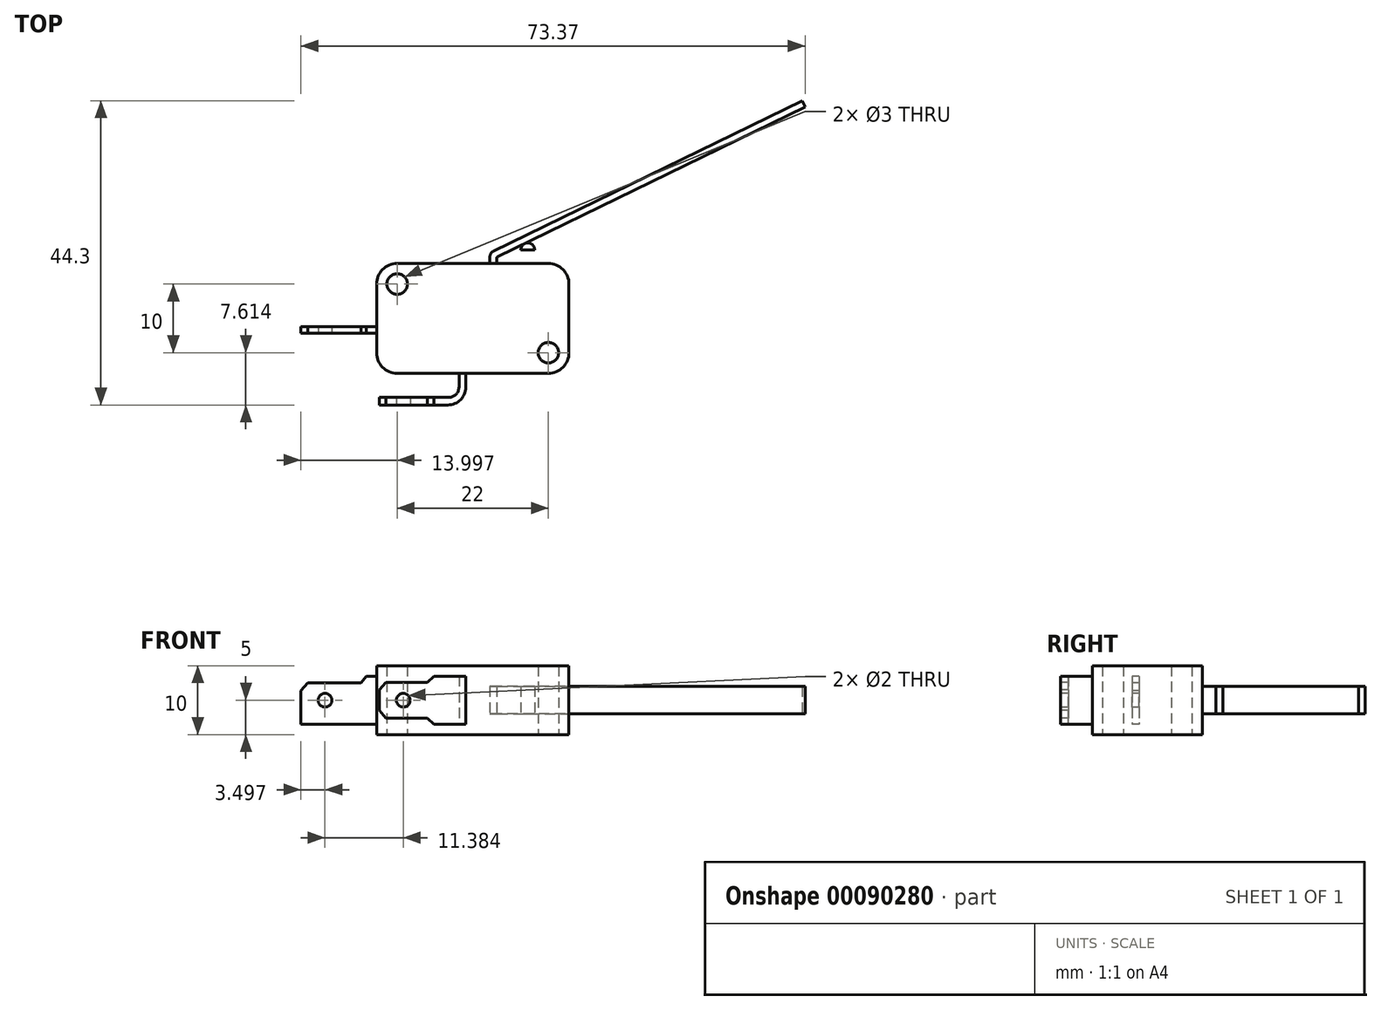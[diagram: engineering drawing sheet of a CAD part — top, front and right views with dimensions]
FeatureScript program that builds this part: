
annotation { "Feature Type Name" : "Feature", "Feature Type Description" : "" }
export const myFeature = defineFeature(function(context is Context, id is Id, definition is map)
    precondition{}
    {
        {
            var Q0;
            Q0=qCreatedBy(makeId("Top.planeOp"),FACE);
            var sketch = newSketch(context, id + "F0", { "sketchPlane" : qUnion([Q0])});
            skLineSegment(sketch, "E0.bottom", {"start": v(11.18, -8.94) * mm, "end": v(33.18, -8.94) * mm});
            skLineSegment(sketch, "E0.top", {"start": v(11.18, -24.94) * mm, "end": v(33.18, -24.94) * mm});
            skLineSegment(sketch, "E0.left", {"start": v(8.18, -11.94) * mm, "end": v(8.18, -21.94) * mm});
            skLineSegment(sketch, "E0.right", {"start": v(36.18, -11.94) * mm, "end": v(36.18, -21.94) * mm});
            skPoint(sketch, "E1.visualSharp", {"position": v(8.18, -8.94) * mm});
            skArc(sketch, "E1.filletArc", {"start": v(11.18, -8.94) * mm, "mid": v(9.06, -9.81) * mm, "end": v(8.18, -11.94) * mm});
            skPoint(sketch, "E2.visualSharp", {"position": v(8.18, -24.94) * mm});
            skArc(sketch, "E2.filletArc", {"start": v(8.18, -21.94) * mm, "mid": v(9.06, -24.06) * mm, "end": v(11.18, -24.94) * mm});
            skPoint(sketch, "E3.visualSharp", {"position": v(36.18, -24.94) * mm});
            skArc(sketch, "E3.filletArc", {"start": v(33.18, -24.94) * mm, "mid": v(35.3, -24.06) * mm, "end": v(36.18, -21.94) * mm});
            skPoint(sketch, "E4.visualSharp", {"position": v(36.18, -8.94) * mm});
            skArc(sketch, "E4.filletArc", {"start": v(36.18, -11.94) * mm, "mid": v(35.3, -9.81) * mm, "end": v(33.18, -8.94) * mm});
            skCircle(sketch, "E5", {"center": v(11.18, -11.94) * mm, "radius": 1.5 * mm});
            skCircle(sketch, "E6", {"center": v(33.18, -21.94) * mm, "radius": 1.5 * mm});
            skLineSegment(sketch, "E7.bottom", {"start": v(29.18, -8.94) * mm, "end": v(31.18, -8.94) * mm});
            skLineSegment(sketch, "E7.top", {"start": v(29.18, -6.94) * mm, "end": v(31.18, -6.94) * mm});
            skLineSegment(sketch, "E7.left", {"start": v(29.18, -8.94) * mm, "end": v(29.18, -6.94) * mm});
            skLineSegment(sketch, "E7.right", {"start": v(31.18, -8.94) * mm, "end": v(31.18, -6.94) * mm});
            skArc(sketch, "E8", {"start": v(31.18, -6.94) * mm, "mid": v(30.18, -5.94) * mm, "end": v(29.18, -6.94) * mm});
            skLineSegment(sketch, "E9", {"start": v(25.68, -8.94) * mm, "end": v(25.68, -8.1) * mm});
            skLineSegment(sketch, "E10", {"start": v(25.76, -7.98) * mm, "end": v(70.55, 13.85) * mm});
            skLineSegment(sketch, "E11", {"start": v(70.55, 13.85) * mm, "end": v(70.12, 14.75) * mm});
            skLineSegment(sketch, "E12", {"start": v(70.12, 14.75) * mm, "end": v(25.17, -7.15) * mm});
            skLineSegment(sketch, "E13", {"start": v(24.68, -7.94) * mm, "end": v(24.68, -8.94) * mm});
            skPoint(sketch, "E14.visualSharp", {"position": v(24.68, -7.4) * mm});
            skArc(sketch, "E14.filletArc", {"start": v(25.17, -7.15) * mm, "mid": v(24.8, -7.47) * mm, "end": v(24.68, -7.94) * mm});
            skPoint(sketch, "E15.visualSharp", {"position": v(25.68, -8.02) * mm});
            skArc(sketch, "E15.filletArc", {"start": v(25.76, -7.98) * mm, "mid": v(25.7, -8.03) * mm, "end": v(25.68, -8.1) * mm});
            skLineSegment(sketch, "E16.bottom", {"start": v(8.18, -19.12) * mm, "end": v(-2.82, -19.12) * mm});
            skLineSegment(sketch, "E16.top", {"start": v(8.18, -18.12) * mm, "end": v(-2.82, -18.12) * mm});
            skLineSegment(sketch, "E16.left", {"start": v(8.18, -19.12) * mm, "end": v(8.18, -18.12) * mm});
            skLineSegment(sketch, "E16.right", {"start": v(-2.82, -19.12) * mm, "end": v(-2.82, -18.12) * mm});
            skLineSegment(sketch, "E17", {"start": v(21.18, -24.94) * mm, "end": v(21.18, -26.94) * mm});
            skLineSegment(sketch, "E18", {"start": v(18.56, -29.55) * mm, "end": v(8.56, -29.55) * mm});
            skLineSegment(sketch, "E19", {"start": v(8.56, -29.55) * mm, "end": v(8.56, -28.44) * mm});
            skLineSegment(sketch, "E20", {"start": v(8.56, -28.44) * mm, "end": v(18.68, -28.44) * mm});
            skLineSegment(sketch, "E21", {"start": v(20.18, -26.94) * mm, "end": v(20.18, -24.94) * mm});
            skPoint(sketch, "E22.visualSharp", {"position": v(21.18, -29.55) * mm});
            skArc(sketch, "E22.filletArc", {"start": v(18.56, -29.55) * mm, "mid": v(20.41, -28.79) * mm, "end": v(21.18, -26.94) * mm});
            skPoint(sketch, "E23.visualSharp", {"position": v(20.18, -28.44) * mm});
            skArc(sketch, "E23.filletArc", {"start": v(18.68, -28.44) * mm, "mid": v(19.74, -28) * mm, "end": v(20.18, -26.94) * mm});
            skLineSegment(sketch, "E24", {"start": v(15.13, -28.44) * mm, "end": v(15.13, -24.94) * mm});
            skSolve(sketch);
        }
        {
            var Q0;
            Q0=makeQuery(id+"F0.imprint","IMPRINT",FACE,{"disambiguationData":[TD([[makeQuery(id+"F0.imprint","IMPRINT",EDGE,{"derivedFrom":sQuery(id+"F0.wireOp",EDGE,"E0.right")}),-1.0]])]});
            extrude(context, id + "F1", {"entities" : qUnion([Q0]), "depth" : 5 * mm, "hasSecondDirection" : true, "secondDirectionOppositeDirection" : true, "secondDirectionDepth" : 5 * mm});
        }
        {
            var Q0;
            Q0=makeQuery(id+"F0.imprint","IMPRINT",FACE,{"disambiguationData":[TD([[makeQuery(id+"F0.imprint","IMPRINT",EDGE,{"derivedFrom":sQuery(id+"F0.wireOp",EDGE,"E7.bottom")}),1.0]])]});
            var Q1;
            {var subQ0=sQuery(id+"F0.wireOp",EDGE,"E7.top");Q1=makeQuery(id+"F0.imprint","IMPRINT",FACE,{"disambiguationData":[TD([[makeQuery(id+"F0.imprint","IMPRINT",EDGE,{"derivedFrom":subQ0}),1.0]])]});}
            extrude(context, id + "F2", {"entities" : qUnion([Q0, Q1]), "depth" : 2 * mm, "hasSecondDirection" : true, "secondDirectionOppositeDirection" : true, "secondDirectionDepth" : 2 * mm});
        }
        {
            var Q0;
            {var subQ4=sQuery(id+"F0.wireOp",EDGE,"E9");Q0=makeQuery(id+"F0.imprint","IMPRINT",FACE,{"disambiguationData":[TD([[makeQuery(id+"F0.imprint","IMPRINT",EDGE,{"derivedFrom":subQ4}),1.0]])]});}
            extrude(context, id + "F3", {"entities" : qUnion([Q0]), "depth" : 2 * mm, "hasSecondDirection" : true, "secondDirectionOppositeDirection" : true, "secondDirectionDepth" : 2 * mm});
        }
        {
            var Q0;
            {var subQ1=sQuery(id+"F0.wireOp",EDGE,"E17");Q0=makeQuery(id+"F0.imprint","IMPRINT",FACE,{"disambiguationData":[TD([[makeQuery(id+"F0.imprint","IMPRINT",EDGE,{"derivedFrom":subQ1}),-1.0]])]});}
            extrude(context, id + "F4", {"entities" : qUnion([Q0]), "depth" : 3.5 * mm, "hasSecondDirection" : true, "secondDirectionOppositeDirection" : true, "secondDirectionDepth" : 3.5 * mm});
        }
        {
            var Q0;
            Q0=makeQuery(id+"F0.imprint","IMPRINT",FACE,{"disambiguationData":[TD([[makeQuery(id+"F0.imprint","IMPRINT",EDGE,{"derivedFrom":sQuery(id+"F0.wireOp",EDGE,"E16.bottom")}),-1.0]])]});
            extrude(context, id + "F5", {"entities" : qUnion([Q0]), "depth" : 3.5 * mm, "hasSecondDirection" : true, "secondDirectionOppositeDirection" : true, "secondDirectionDepth" : 3.5 * mm});
        }
        {
            var Q0;
            Q0=makeQuery(id+"F4.opExtrude","SWEPT_FACE",FACE,{"disambiguationData":[OSD([sQuery(id+"F0.wireOp",EDGE,"E18")])]});
            var sketch = newSketch(context, id + "F6", { "sketchPlane" : qUnion([Q0])});
            skCircle(sketch, "E25", {"center": v(12.06, 0) * mm, "radius": 1 * mm});
            skLineSegment(sketch, "E26", {"start": v(16.52, 3.5) * mm, "end": v(15.56, 2.62) * mm});
            skLineSegment(sketch, "E27", {"start": v(15.56, 2.62) * mm, "end": v(9.56, 2.62) * mm});
            skLineSegment(sketch, "E28", {"start": v(9.56, 2.62) * mm, "end": v(8.56, 1.5) * mm});
            skLineSegment(sketch, "E29", {"start": v(8.56, 1.5) * mm, "end": v(8.56, -1.5) * mm});
            skLineSegment(sketch, "E30", {"start": v(8.56, -1.5) * mm, "end": v(9.56, -2.62) * mm});
            skLineSegment(sketch, "E31", {"start": v(9.56, -2.62) * mm, "end": v(15.56, -2.62) * mm});
            skLineSegment(sketch, "E32", {"start": v(15.56, -2.62) * mm, "end": v(16.52, -3.5) * mm});
            skSolve(sketch);
        }
        {
            var Q0;
            {var subQ4=sQuery(id+"F6.wireOp",EDGE,"E30");Q0=makeQuery(id+"F6.imprint","IMPRINT",FACE,{"disambiguationData":[TD([[makeQuery(id+"F6.imprint","IMPRINT",EDGE,{"derivedFrom":subQ4}),-1.0]])]});}
            var Q1;
            {var subQ5=sQuery(id+"F6.wireOp",EDGE,"E26");Q1=makeQuery(id+"F6.imprint","IMPRINT",FACE,{"disambiguationData":[TD([[makeQuery(id+"F6.imprint","IMPRINT",EDGE,{"derivedFrom":subQ5}),-1.0]])]});}
            var Q2;
            Q2=makeQuery(id+"F6.imprint","IMPRINT",FACE,{"disambiguationData":[TD([[makeQuery(id+"F6.imprint","IMPRINT",EDGE,{"derivedFrom":sQuery(id+"F6.wireOp",EDGE,"E25")}),1.0]])]});
            extrude(context, id + "F7", {"entities" : qUnion([Q0, Q1, Q2]), "operationType" : NewBodyOperationType.REMOVE, "oppositeDirection" : true, "depth" : 3.08 * mm});
        }
        {
            var Q0;
            Q0=makeQuery(id+"F4.opExtrude","SWEPT_FACE",FACE,{"disambiguationData":[OSD([sQuery(id+"F0.wireOp",EDGE,"E18")])]});
            var sketch = newSketch(context, id + "F8", { "sketchPlane" : qUnion([Q0])});
            skCircle(sketch, "E33", {"center": v(0.68, 0) * mm, "radius": 1 * mm});
            skLineSegment(sketch, "E34", {"start": v(8.18, -3.5) * mm, "end": v(8.18, 3.5) * mm});
            skLineSegment(sketch, "E35", {"start": v(8.18, 3.5) * mm, "end": v(6.68, 3.5) * mm});
            skLineSegment(sketch, "E36", {"start": v(6.68, 3.5) * mm, "end": v(5.93, 2.5) * mm});
            skLineSegment(sketch, "E37", {"start": v(5.93, 2.5) * mm, "end": v(-1.82, 2.5) * mm});
            skLineSegment(sketch, "E38", {"start": v(-1.82, 2.5) * mm, "end": v(-2.82, 1.37) * mm});
            skLineSegment(sketch, "E39", {"start": v(-2.82, 1.37) * mm, "end": v(-2.82, -1.38) * mm});
            skLineSegment(sketch, "E40", {"start": v(-2.82, -1.38) * mm, "end": v(-1.82, -2.5) * mm});
            skLineSegment(sketch, "E41", {"start": v(-1.82, -2.5) * mm, "end": v(5.93, -2.5) * mm});
            skLineSegment(sketch, "E42", {"start": v(5.93, -2.5) * mm, "end": v(6.68, -3.5) * mm});
            skLineSegment(sketch, "E43", {"start": v(6.68, -3.5) * mm, "end": v(8.18, -3.5) * mm});
            skLineSegment(sketch, "E44", {"start": v(6.68, 3.5) * mm, "end": v(-2.82, 3.5) * mm});
            skLineSegment(sketch, "E45", {"start": v(-2.82, 3.5) * mm, "end": v(-2.82, 1.37) * mm});
            skLineSegment(sketch, "E46", {"start": v(-2.82, -1.38) * mm, "end": v(-2.82, -3.5) * mm});
            skLineSegment(sketch, "E47", {"start": v(-2.82, -3.5) * mm, "end": v(6.68, -3.5) * mm});
            skLineSegment(sketch, "E48", {"start": v(5.93, -2.5) * mm, "end": v(-1.82, -2.5) * mm});
            skLineSegment(sketch, "E49", {"start": v(6.68, -3.5) * mm, "end": v(-2.82, -3.5) * mm});
            skLineSegment(sketch, "E50", {"start": v(-2.82, -3.5) * mm, "end": v(-2.82, -1.38) * mm});
            skSolve(sketch);
        }
        {
            var Q0;
            Q0=makeQuery(id+"F8.imprint","IMPRINT",FACE,{"disambiguationData":[TD([[makeQuery(id+"F8.imprint","IMPRINT",EDGE,{"derivedFrom":sQuery(id+"F8.wireOp",EDGE,"E36")}),-1.0]])]});
            var Q1;
            Q1=makeQuery(id+"F8.imprint","IMPRINT",FACE,{"disambiguationData":[TD([[makeQuery(id+"F8.imprint","IMPRINT",EDGE,{"derivedFrom":sQuery(id+"F8.wireOp",EDGE,"E33")}),1.0]])]});
            var Q2;
            Q2=makeQuery(id+"F8.imprint","IMPRINT",FACE,{"disambiguationData":[TD([[makeQuery(id+"F8.imprint","IMPRINT",EDGE,{"derivedFrom":sQuery(id+"F8.wireOp",EDGE,"E40")}),-1.0]])]});
            extrude(context, id + "F9", {"entities" : qUnion([Q0, Q1, Q2]), "operationType" : NewBodyOperationType.REMOVE, "oppositeDirection" : true, "depth" : 25 * mm});
        }
    });
